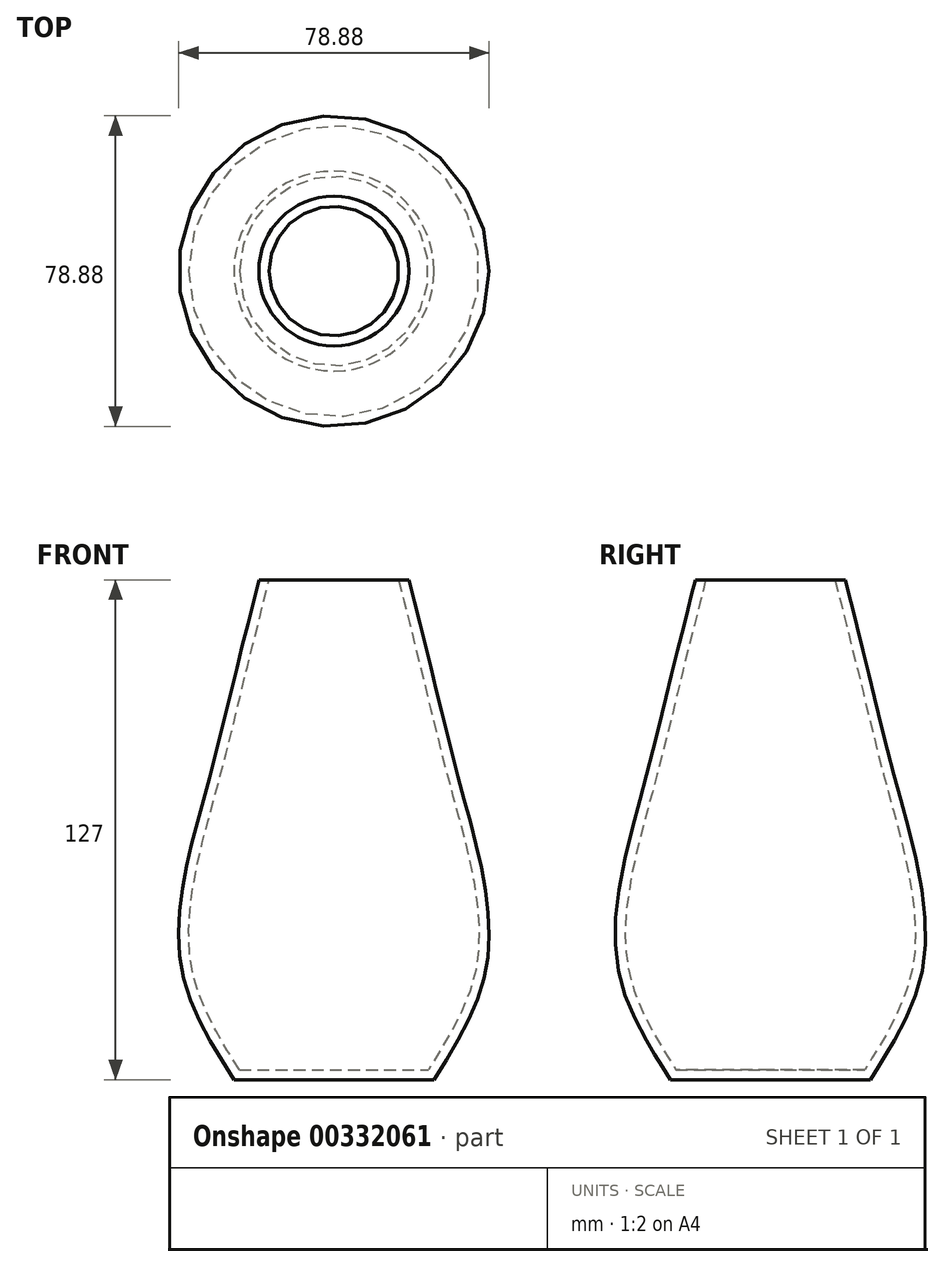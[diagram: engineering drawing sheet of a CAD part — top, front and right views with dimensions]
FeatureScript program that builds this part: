
annotation { "Feature Type Name" : "Feature", "Feature Type Description" : "" }
export const myFeature = defineFeature(function(context is Context, id is Id, definition is map)
    precondition{}
    {
        {
            var Q0;
            Q0=qCreatedBy(makeId("Top.planeOp"),FACE);
            cPlane(context, id + "F0", {"entities" : qUnion([Q0]), "cplaneType" : CPlaneType.OFFSET, "offset" : 25.4 * mm, "width" : 152.4 * mm, "height" : 152.4 * mm});
        }
        {
            var Q0;
            Q0=qCreatedBy(id+"F0.planeOp",FACE);
            cPlane(context, id + "F1", {"entities" : qUnion([Q0]), "cplaneType" : CPlaneType.OFFSET, "offset" : 50.8 * mm, "width" : 152.4 * mm, "height" : 152.4 * mm});
        }
        {
            var Q0;
            Q0=qCreatedBy(id+"F1.planeOp",FACE);
            cPlane(context, id + "F2", {"entities" : qUnion([Q0]), "cplaneType" : CPlaneType.OFFSET, "offset" : 25.4 * mm, "width" : 152.4 * mm, "height" : 152.4 * mm});
        }
        {
            var Q0;
            Q0=qCreatedBy(id+"F2.planeOp",FACE);
            cPlane(context, id + "F3", {"entities" : qUnion([Q0]), "cplaneType" : CPlaneType.OFFSET, "offset" : 25.4 * mm, "width" : 152.4 * mm, "height" : 152.4 * mm});
        }
        {
            var Q0;
            Q0=qCreatedBy(makeId("Top.planeOp"),FACE);
            var sketch = newSketch(context, id + "F4", { "sketchPlane" : qUnion([Q0])});
            skCircle(sketch, "E0", {"center": v(0, 0) * mm, "radius": 25.4 * mm});
            skSolve(sketch);
        }
        {
            var Q0;
            Q0=qCreatedBy(id+"F0.planeOp",FACE);
            var sketch = newSketch(context, id + "F5", { "sketchPlane" : qUnion([Q0])});
            skCircle(sketch, "E1", {"center": v(0, 0) * mm, "radius": 38.1 * mm});
            skSolve(sketch);
        }
        {
            var Q0;
            Q0=qCreatedBy(id+"F1.planeOp",FACE);
            var sketch = newSketch(context, id + "F6", { "sketchPlane" : qUnion([Q0])});
            skCircle(sketch, "E2", {"center": v(0, 0) * mm, "radius": 31.75 * mm});
            skSolve(sketch);
        }
        {
            var Q0;
            Q0=qCreatedBy(id+"F2.planeOp",FACE);
            var sketch = newSketch(context, id + "F7", { "sketchPlane" : qUnion([Q0])});
            skCircle(sketch, "E3", {"center": v(0, 0) * mm, "radius": 25.4 * mm});
            skSolve(sketch);
        }
        {
            var Q0;
            Q0=qCreatedBy(id+"F3.planeOp",FACE);
            var sketch = newSketch(context, id + "F8", { "sketchPlane" : qUnion([Q0])});
            skCircle(sketch, "E4", {"center": v(0, 0) * mm, "radius": 19.05 * mm});
            skSolve(sketch);
        }
        {
            var Q0;
            Q0=makeQuery(id+"F4.imprint","IMPRINT",FACE,{"disambiguationData":[TD([[makeQuery(id+"F4.imprint","IMPRINT",EDGE,{"derivedFrom":sQuery(id+"F4.wireOp",EDGE,"E0")}),1.0]])]});
            var Q1;
            Q1=makeQuery(id+"F5.imprint","IMPRINT",FACE,{"disambiguationData":[TD([[makeQuery(id+"F5.imprint","IMPRINT",EDGE,{"derivedFrom":sQuery(id+"F5.wireOp",EDGE,"E1")}),1.0]])]});
            var Q2;
            Q2=makeQuery(id+"F6.imprint","IMPRINT",FACE,{"disambiguationData":[TD([[makeQuery(id+"F6.imprint","IMPRINT",EDGE,{"derivedFrom":sQuery(id+"F6.wireOp",EDGE,"E2")}),1.0]])]});
            var Q3;
            Q3=makeQuery(id+"F7.imprint","IMPRINT",FACE,{"disambiguationData":[TD([[makeQuery(id+"F7.imprint","IMPRINT",EDGE,{"derivedFrom":sQuery(id+"F7.wireOp",EDGE,"E3")}),1.0]])]});
            var Q4;
            Q4=makeQuery(id+"F8.imprint","IMPRINT",FACE,{"disambiguationData":[TD([[makeQuery(id+"F8.imprint","IMPRINT",EDGE,{"derivedFrom":sQuery(id+"F8.wireOp",EDGE,"E4")}),1.0]])]});
            loft(context, id + "F9", {"sheetProfilesArray" : [{ "sheetProfileEntities" : qUnion([Q0]) }, { "sheetProfileEntities" : qUnion([Q1]) }, { "sheetProfileEntities" : qUnion([Q2]) }, { "sheetProfileEntities" : qUnion([Q3]) }, { "sheetProfileEntities" : qUnion([Q4]) }]});
        }
        {
            var Q0;
            Q0=makeQuery(id+"F9.opLoft","CAP_FACE",FACE,{"disambiguationData":[OSD([makeQuery(id+"F8.imprint","IMPRINT",FACE,{"disambiguationData":[TD([[makeQuery(id+"F8.imprint","IMPRINT",EDGE,{"derivedFrom":sQuery(id+"F8.wireOp",EDGE,"E4")}),1.0]])]})])],"isStart":true});
            shell(context, id + "F10", {"entities" : qUnion([Q0]), "thickness" : 2.54 * mm});
        }
    });
